# Revit family: LUXI_PANEL LIGHT_LG-E
name_source: partatom
category: Apparecchi per illuminazione
revit_build: Autodesk Revit 2016 (Build: 20161004_0715(x64)
units: mm (PartAtom-declared; Revit-internal decimal feet)

## family parameters
Condiviso = No
Host = Superficie
Numero OmniClass = 23.80.70.00
Punto di calcolo locali = Sì
Quota connettore circolare = Usa diametro
Sorgente d'illuminazione = Sì
Taglio con vuoti quando caricato = No
Tipo di parte = Normale
Titolo OmniClass = Lighting

## types (2) — shared parameters
Angolo inclinazione = -90.00°
CRI = ≥90 (typ.)
Carico apparente = 36 VA
Certifications = CE / RohS
Color = White
Descrizione = LED panel, high efficiency
Dimming = 1-10V / DALI / PUSH DIM selectable from dip-switch
Dust and water protection rating = IP20, IP 44 (front)
Energy class = A++
Filtro dei colori = 16777215
H = 11 mm  [stored 0.0360892 ft]
IFCExportAs = IFCLightFixtureType
Impact rating = IK07 (2 Joule)
Installation = Recessed / ceiling / suspended
Lifetime = L70B20 60.000h
Light distribution = Edge light
Light source = LED SMD
Masterformat 2016 code = 26.50.00
Masterformat 2016 description = Lighting
Material 1 = High Trasmittance Microprismatic Technopolimer
Material 2 = Extruded Aluminum_White
Material 3 = Sheet Steel
Modello = LG-E Series | Panel Light
OFF1 = 38 mm  [stored 0.124672 ft]
Operating temperature = 0°C / +40°C
Optics = Microprismatic panel UGR≤19
Photobiological risk group = RG0
Power factor = ≥0,95 (typ.)
Power supply = Included, dimmable
Produttore = Luxi Illuminazione S.r.l.
Prospetto di default = 2000 mm  [stored 6.56168 ft]
Protection class = II
Rated supply voltage = 220-240V AC / 50-60 Hz
Rendi la forma visibile nel rendering = No
Review = 3
Step MacAdam (SDCM) = <4
URL = https://www.luxi.lighting
Uniclass 2015 code = EF_70_80
Uniclass 2015 description = Lighting
Variazione temperatura colore lampada con luminosità attenuata = <Nessuno>
Warranty = 5 years
Wattage = 36 W

## per-type parameters (varying)
| type | Emetti da larghezza rettangolo | Emetti da lunghezza rettangolo | File diagramma fotometrico | Length | Size | Weight | Width |
| LPGE036660W940DA | 519 mm  [stored 1.70276 ft] | 519 mm  [stored 1.70276 ft] | LPGE036660W940DA Luxi SERIE LG-E CRI90 DIM 60x60 36W 4000K.IES | 595 mm  [stored 1.9521 ft] | 595x595x11 | 3.60 kg | 595 mm  [stored 1.9521 ft] |
| LPGE036312W940DA | 219 mm | 1119 mm  [stored 3.67126 ft] | LPGE036312W940DA Luxi SERIE LG-E CRI90 DIM 30x120 36W 4000K.IES | 1195 mm  [stored 3.9206 ft] | 295x1295x11 | 3.80 kg | 295 mm  [stored 0.967848 ft] |

note: column(s) folded — value = type name in every type: Code

note: [stored X ft] marks values corroborated as IEEE doubles in the binary element streams (Revit-internal decimal feet)
